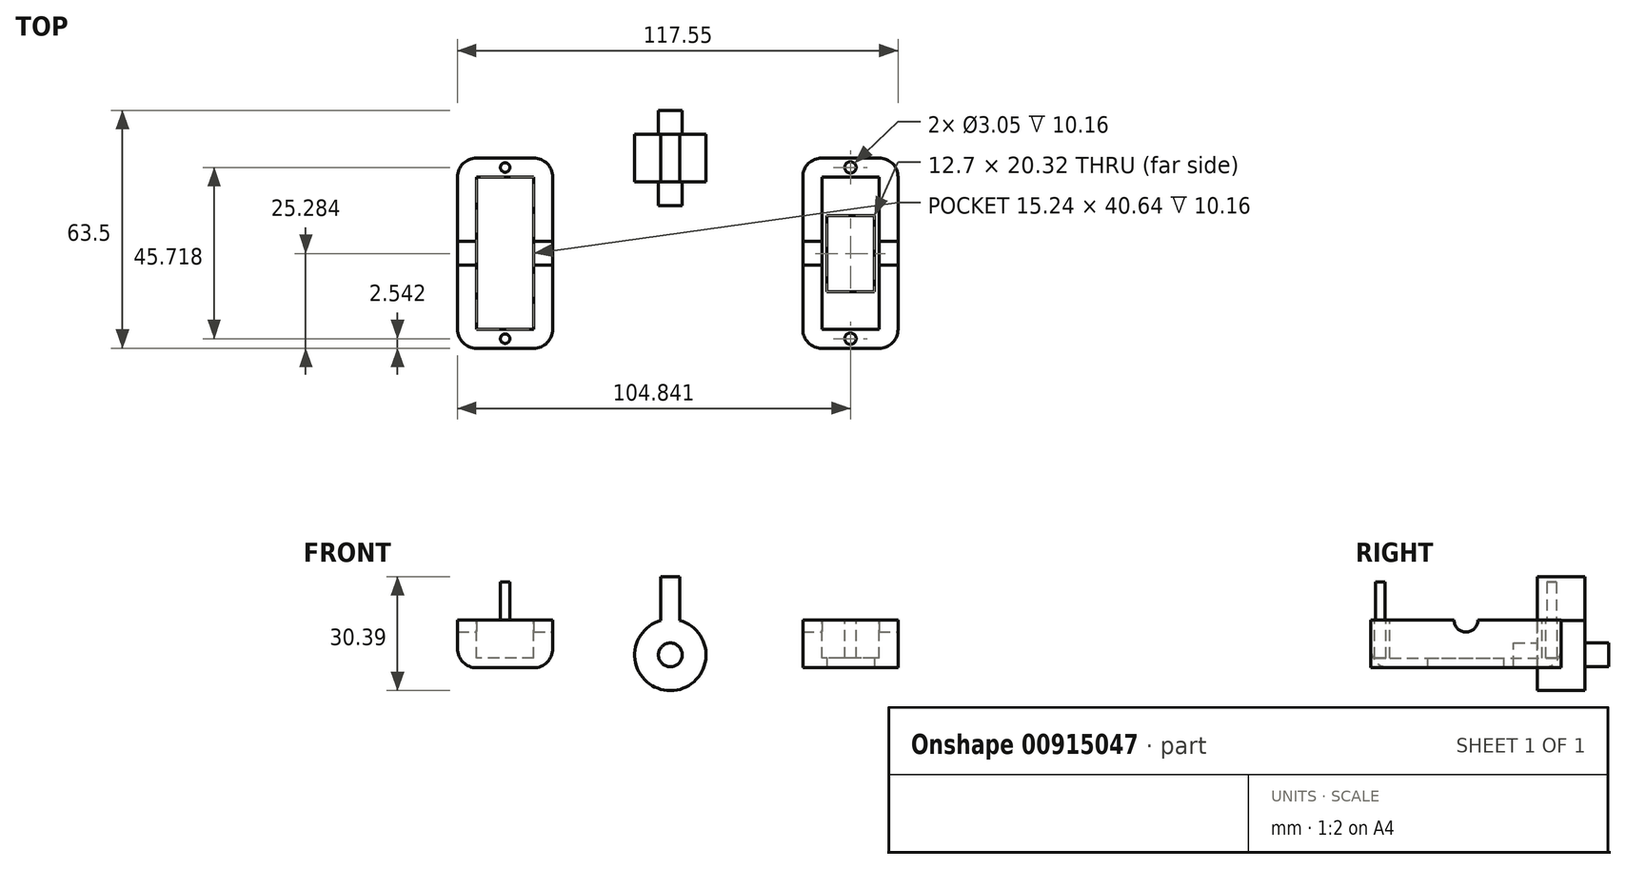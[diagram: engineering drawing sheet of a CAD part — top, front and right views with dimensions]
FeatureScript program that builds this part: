
annotation { "Feature Type Name" : "Feature", "Feature Type Description" : "" }
export const myFeature = defineFeature(function(context is Context, id is Id, definition is map)
    precondition{}
    {
        {
            var Q0;
            Q0=qCreatedBy(makeId("Front.planeOp"),FACE);
            var sketch = newSketch(context, id + "F0", { "sketchPlane" : qUnion([Q0])});
            skLineSegment(sketch, "E0", {"start": v(-56.79, 0) * mm, "end": v(-31.39, 0) * mm});
            skLineSegment(sketch, "E1", {"start": v(-31.39, 0) * mm, "end": v(-31.39, -12.7) * mm});
            skLineSegment(sketch, "E2", {"start": v(-31.39, -12.7) * mm, "end": v(-56.79, -12.7) * mm});
            skLineSegment(sketch, "E3", {"start": v(-56.79, -12.7) * mm, "end": v(-56.79, 0) * mm});
            skLineSegment(sketch, "E4", {"start": v(35.35, 0) * mm, "end": v(60.76, 0) * mm});
            skLineSegment(sketch, "E5", {"start": v(60.76, 0) * mm, "end": v(60.76, -12.7) * mm});
            skLineSegment(sketch, "E6", {"start": v(60.76, -12.7) * mm, "end": v(35.35, -12.7) * mm});
            skLineSegment(sketch, "E7", {"start": v(35.35, -12.7) * mm, "end": v(35.35, 0) * mm});
            skCircle(sketch, "E8", {"center": v(0, -9.27) * mm, "radius": 3.18 * mm});
            skCircle(sketch, "E9.0", {"center": v(0, -9.27) * mm, "radius": 9.52 * mm});
            skLineSegment(sketch, "E10", {"start": v(0, 0.26) * mm, "end": v(0, 9.15) * mm});
            skLineSegment(sketch, "E11", {"start": v(-2.54, 11.6) * mm, "end": v(-2.54, -0.09) * mm});
            skLineSegment(sketch, "E12", {"start": v(2.54, 9.15) * mm, "end": v(2.54, -0.09) * mm});
            skLineSegment(sketch, "E13", {"start": v(0, 9.15) * mm, "end": v(0, 11.6) * mm});
            skLineSegment(sketch, "E14", {"start": v(0, 11.6) * mm, "end": v(-2.54, 11.6) * mm});
            skLineSegment(sketch, "E15", {"start": v(2.54, 9.15) * mm, "end": v(2.54, 11.6) * mm});
            skLineSegment(sketch, "E16", {"start": v(2.54, 11.6) * mm, "end": v(0, 11.6) * mm});
            skSolve(sketch);
        }
        {
            var Q0;
            Q0=makeQuery(id+"F0.imprint","IMPRINT",FACE,{"disambiguationData":[TD([[makeQuery(id+"F0.imprint","IMPRINT",EDGE,{"derivedFrom":sQuery(id+"F0.wireOp",EDGE,"E4")}),-1.0]])]});
            var Q1;
            Q1=makeQuery(id+"F0.imprint","IMPRINT",FACE,{"disambiguationData":[TD([[makeQuery(id+"F0.imprint","IMPRINT",EDGE,{"derivedFrom":sQuery(id+"F0.wireOp",EDGE,"E0")}),-1.0]])]});
            extrude(context, id + "F1", {"entities" : qUnion([Q0, Q1]), "depth" : 50.8 * mm});
        }
        {
            var Q0;
            Q0=qCreatedBy(makeId("Top.planeOp"),FACE);
            var sketch = newSketch(context, id + "F2", { "sketchPlane" : qUnion([Q0])});
            skLineSegment(sketch, "E17.0", {"start": v(-36.47, -5.08) * mm, "end": v(-51.7, -5.08) * mm});
            skLineSegment(sketch, "E17.1", {"start": v(-36.47, -45.72) * mm, "end": v(-36.47, -5.08) * mm});
            skLineSegment(sketch, "E17.2", {"start": v(-51.7, -45.72) * mm, "end": v(-36.47, -45.72) * mm});
            skLineSegment(sketch, "E17.3", {"start": v(-51.7, -5.08) * mm, "end": v(-51.7, -45.72) * mm});
            skLineSegment(sketch, "E18.0", {"start": v(55.68, -5.08) * mm, "end": v(40.43, -5.08) * mm});
            skLineSegment(sketch, "E18.1", {"start": v(55.68, -45.72) * mm, "end": v(55.68, -5.08) * mm});
            skLineSegment(sketch, "E18.2", {"start": v(40.43, -45.72) * mm, "end": v(55.68, -45.72) * mm});
            skLineSegment(sketch, "E18.3", {"start": v(40.43, -5.08) * mm, "end": v(40.43, -45.72) * mm});
            skCircle(sketch, "E19", {"center": v(-44.09, -48.25) * mm, "radius": 1.27 * mm});
            skCircle(sketch, "E20", {"center": v(-44.09, -2.54) * mm, "radius": 1.27 * mm});
            skCircle(sketch, "E21", {"center": v(48.05, -2.54) * mm, "radius": 1.52 * mm});
            skCircle(sketch, "E22", {"center": v(48.05, -48.26) * mm, "radius": 1.52 * mm});
            skSolve(sketch);
        }
        {
            var Q0;
            Q0=makeQuery(id+"F2.imprint","IMPRINT",FACE,{"disambiguationData":[TD([[makeQuery(id+"F2.imprint","IMPRINT",EDGE,{"derivedFrom":sQuery(id+"F2.wireOp",EDGE,"E17.0")}),1.0]])]});
            extrude(context, id + "F3", {"entities" : qUnion([Q0]), "operationType" : NewBodyOperationType.REMOVE, "oppositeDirection" : true, "depth" : 10.16 * mm});
        }
        {
            var Q0;
            Q0=makeQuery(id+"F2.imprint","IMPRINT",FACE,{"disambiguationData":[TD([[makeQuery(id+"F2.imprint","IMPRINT",EDGE,{"derivedFrom":sQuery(id+"F2.wireOp",EDGE,"E18.0")}),1.0]])]});
            extrude(context, id + "F4", {"entities" : qUnion([Q0]), "operationType" : NewBodyOperationType.REMOVE, "oppositeDirection" : true, "depth" : 10.16 * mm});
        }
        {
            var Q0;
            Q0=makeQuery(id+"F1.opExtrude","SWEPT_FACE",FACE,{"disambiguationData":[OSD([sQuery(id+"F0.wireOp",EDGE,"E1")])]});
            var sketch = newSketch(context, id + "F5", { "sketchPlane" : qUnion([Q0])});
            skCircle(sketch, "E23", {"center": v(-25.4, 0) * mm, "radius": 3.18 * mm});
            skSolve(sketch);
        }
        {
            var Q0;
            {var subQ0=sQuery(id+"F5.wireOp",EDGE,"E23");var subQ1=makeQuery(id+"F1.opExtrude","SWEPT_EDGE",EDGE,{"disambiguationData":[OSD([sQuery(id+"F0.wireOp",EDGE,"E0"),sQuery(id+"F0.wireOp",EDGE,"E1")])]});var subQ2=makeQuery(id+"F5.imprint","INTERSECT",VERTEX,{"disambiguationData":[OD(0.0)],"derivedFrom":[subQ1,subQ0]});Q0=makeQuery(id+"F5.imprint","IMPRINT",FACE,{"disambiguationData":[TD([[makeQuery(id+"F5.imprint","IMPRINT",EDGE,{"disambiguationData":[TD([[subQ2,1.0]])],"derivedFrom":subQ0}),1.0]])]});}
            extrude(context, id + "F6", {"entities" : qUnion([Q0]), "operationType" : NewBodyOperationType.REMOVE, "oppositeDirection" : true, "depth" : 25.4 * mm});
        }
        {
            var Q0;
            Q0=makeQuery(id+"F1.opExtrude","SWEPT_FACE",FACE,{"disambiguationData":[OSD([sQuery(id+"F0.wireOp",EDGE,"E5")])]});
            var sketch = newSketch(context, id + "F7", { "sketchPlane" : qUnion([Q0])});
            skCircle(sketch, "E24", {"center": v(-25.4, 0) * mm, "radius": 3.18 * mm});
            skSolve(sketch);
        }
        {
            var Q0;
            {var subQ0=sQuery(id+"F7.wireOp",EDGE,"E24");var subQ1=makeQuery(id+"F1.opExtrude","SWEPT_EDGE",EDGE,{"disambiguationData":[OSD([sQuery(id+"F0.wireOp",EDGE,"E4"),sQuery(id+"F0.wireOp",EDGE,"E5")])]});var subQ2=makeQuery(id+"F7.imprint","INTERSECT",VERTEX,{"disambiguationData":[OD(0.0)],"derivedFrom":[subQ1,subQ0]});Q0=makeQuery(id+"F7.imprint","IMPRINT",FACE,{"disambiguationData":[TD([[makeQuery(id+"F7.imprint","IMPRINT",EDGE,{"disambiguationData":[TD([[subQ2,1.0]])],"derivedFrom":subQ0}),1.0]])]});}
            extrude(context, id + "F8", {"entities" : qUnion([Q0]), "operationType" : NewBodyOperationType.REMOVE, "oppositeDirection" : true, "depth" : 25.4 * mm});
        }
        {
            var Q0;
            Q0=makeQuery(id+"F1.opExtrude","SWEPT_FACE",FACE,{"disambiguationData":[OSD([sQuery(id+"F0.wireOp",EDGE,"E6")])]});
            var sketch = newSketch(context, id + "F9", { "sketchPlane" : qUnion([Q0])});
            skLineSegment(sketch, "E25", {"start": v(41.7, 25.52) * mm, "end": v(41.7, 15.36) * mm});
            skLineSegment(sketch, "E26", {"start": v(41.7, 25.52) * mm, "end": v(41.7, 35.68) * mm});
            skLineSegment(sketch, "E27", {"start": v(54.4, 15.36) * mm, "end": v(54.4, 25.52) * mm});
            skLineSegment(sketch, "E28", {"start": v(41.7, 35.68) * mm, "end": v(54.4, 35.68) * mm});
            skLineSegment(sketch, "E29", {"start": v(54.4, 35.68) * mm, "end": v(54.4, 25.52) * mm});
            skLineSegment(sketch, "E30", {"start": v(41.7, 15.36) * mm, "end": v(54.4, 15.36) * mm});
            skLineSegment(sketch, "E31", {"start": v(41.7, 25.52) * mm, "end": v(54.4, 25.52) * mm});
            skSolve(sketch);
        }
        {
            var Q0;
            Q0=makeQuery(id+"F1.opExtrude","CAP_EDGE",EDGE,{"disambiguationData":[OSD([sQuery(id+"F0.wireOp",EDGE,"E1")])],"isStart":false});
            var Q1;
            Q1=makeQuery(id+"F1.opExtrude","CAP_EDGE",EDGE,{"disambiguationData":[OSD([sQuery(id+"F0.wireOp",EDGE,"E3")])],"isStart":false});
            var Q2;
            Q2=makeQuery(id+"F1.opExtrude","CAP_EDGE",EDGE,{"disambiguationData":[OSD([sQuery(id+"F0.wireOp",EDGE,"E2")])],"isStart":false});
            var Q3;
            Q3=makeQuery(id+"F1.opExtrude","SWEPT_EDGE",EDGE,{"disambiguationData":[OSD([sQuery(id+"F0.wireOp",EDGE,"E2"),sQuery(id+"F0.wireOp",EDGE,"E3")])]});
            var Q4;
            Q4=makeQuery(id+"F1.opExtrude","CAP_EDGE",EDGE,{"disambiguationData":[OSD([sQuery(id+"F0.wireOp",EDGE,"E3")])],"isStart":true});
            var Q5;
            Q5=makeQuery(id+"F1.opExtrude","CAP_EDGE",EDGE,{"disambiguationData":[OSD([sQuery(id+"F0.wireOp",EDGE,"E2")])],"isStart":true});
            var Q6;
            Q6=makeQuery(id+"F1.opExtrude","CAP_EDGE",EDGE,{"disambiguationData":[OSD([sQuery(id+"F0.wireOp",EDGE,"E1")])],"isStart":true});
            var Q7;
            Q7=makeQuery(id+"F1.opExtrude","SWEPT_EDGE",EDGE,{"disambiguationData":[OSD([sQuery(id+"F0.wireOp",EDGE,"E1"),sQuery(id+"F0.wireOp",EDGE,"E2")])]});
            fillet(context, id + "F10", {"entities" : qUnion([Q0, Q1, Q2, Q3, Q4, Q5, Q6, Q7]), "radius" : 5.08 * mm, "tangentPropagation" : true, "allowEdgeOverflow" : false});
        }
        {
            var Q0;
            Q0=makeQuery(id+"F0.imprint","IMPRINT",FACE,{"disambiguationData":[TD([[makeQuery(id+"F0.imprint","IMPRINT",EDGE,{"derivedFrom":sQuery(id+"F0.wireOp",EDGE,"E8")}),-1.0]])]});
            var Q1;
            {var subQ0=sQuery(id+"F0.wireOp",EDGE,"E10");Q1=makeQuery(id+"F0.imprint","IMPRINT",FACE,{"disambiguationData":[TD([[makeQuery(id+"F0.imprint","IMPRINT",EDGE,{"derivedFrom":subQ0}),-1.0]])]});}
            var Q2;
            {var subQ0=sQuery(id+"F0.wireOp",EDGE,"E10");Q2=makeQuery(id+"F0.imprint","IMPRINT",FACE,{"disambiguationData":[TD([[makeQuery(id+"F0.imprint","IMPRINT",EDGE,{"derivedFrom":subQ0}),1.0]])]});}
            extrude(context, id + "F11", {"entities" : qUnion([Q0, Q1, Q2]), "endBound" : BoundingType.SYMMETRIC, "depth" : 12.7 * mm, "offsetDistance" : 25.4 * mm});
        }
        {
            var Q0;
            Q0=makeQuery(id+"F0.imprint","IMPRINT",FACE,{"disambiguationData":[TD([[makeQuery(id+"F0.imprint","IMPRINT",EDGE,{"derivedFrom":sQuery(id+"F0.wireOp",EDGE,"E8")}),1.0]])]});
            extrude(context, id + "F12", {"entities" : qUnion([Q0]), "operationType" : NewBodyOperationType.ADD, "endBound" : BoundingType.SYMMETRIC, "depth" : 25.4 * mm, "offsetDistance" : 25.4 * mm});
        }
        {
            var Q0;
            Q0=makeQuery(id+"F2.imprint","IMPRINT",FACE,{"disambiguationData":[TD([[makeQuery(id+"F2.imprint","IMPRINT",EDGE,{"derivedFrom":sQuery(id+"F2.wireOp",EDGE,"E20")}),1.0]])]});
            var Q1;
            Q1=makeQuery(id+"F2.imprint","IMPRINT",FACE,{"disambiguationData":[TD([[makeQuery(id+"F2.imprint","IMPRINT",EDGE,{"derivedFrom":sQuery(id+"F2.wireOp",EDGE,"E19")}),1.0]])]});
            extrude(context, id + "F13", {"entities" : qUnion([Q0, Q1]), "operationType" : NewBodyOperationType.ADD, "depth" : 10.16 * mm, "offsetDistance" : 25.4 * mm});
        }
        {
            var Q0;
            Q0=makeQuery(id+"F2.imprint","IMPRINT",FACE,{"disambiguationData":[TD([[makeQuery(id+"F2.imprint","IMPRINT",EDGE,{"derivedFrom":sQuery(id+"F2.wireOp",EDGE,"E22")}),1.0]])]});
            var Q1;
            Q1=makeQuery(id+"F2.imprint","IMPRINT",FACE,{"disambiguationData":[TD([[makeQuery(id+"F2.imprint","IMPRINT",EDGE,{"derivedFrom":sQuery(id+"F2.wireOp",EDGE,"E21")}),1.0]])]});
            extrude(context, id + "F14", {"entities" : qUnion([Q0, Q1]), "operationType" : NewBodyOperationType.REMOVE, "oppositeDirection" : true, "depth" : 10.16 * mm, "offsetDistance" : 25.4 * mm});
        }
        {
            var Q0;
            Q0=makeQuery(id+"F1.opExtrude","CAP_EDGE",EDGE,{"disambiguationData":[OSD([sQuery(id+"F0.wireOp",EDGE,"E7")])],"isStart":false});
            var Q1;
            Q1=makeQuery(id+"F1.opExtrude","CAP_EDGE",EDGE,{"disambiguationData":[OSD([sQuery(id+"F0.wireOp",EDGE,"E5")])],"isStart":true});
            var Q2;
            Q2=makeQuery(id+"F1.opExtrude","CAP_EDGE",EDGE,{"disambiguationData":[OSD([sQuery(id+"F0.wireOp",EDGE,"E7")])],"isStart":true});
            var Q3;
            Q3=makeQuery(id+"F1.opExtrude","CAP_EDGE",EDGE,{"disambiguationData":[OSD([sQuery(id+"F0.wireOp",EDGE,"E5")])],"isStart":false});
            fillet(context, id + "F15", {"entities" : qUnion([Q0, Q1, Q2, Q3]), "radius" : 5.08 * mm, "tangentPropagation" : true, "allowEdgeOverflow" : false});
        }
        {
            var Q0;
            Q0=makeQuery(id+"F9.imprint","IMPRINT",FACE,{"disambiguationData":[TD([[makeQuery(id+"F9.imprint","IMPRINT",EDGE,{"derivedFrom":sQuery(id+"F9.wireOp",EDGE,"E25")}),1.0]])]});
            var Q1;
            Q1=makeQuery(id+"F9.imprint","IMPRINT",FACE,{"disambiguationData":[TD([[makeQuery(id+"F9.imprint","IMPRINT",EDGE,{"derivedFrom":sQuery(id+"F9.wireOp",EDGE,"E26")}),-1.0]])]});
            extrude(context, id + "F16", {"entities" : qUnion([Q0, Q1]), "operationType" : NewBodyOperationType.REMOVE, "oppositeDirection" : true, "depth" : 25.4 * mm, "offsetDistance" : 25.4 * mm});
        }
    });
